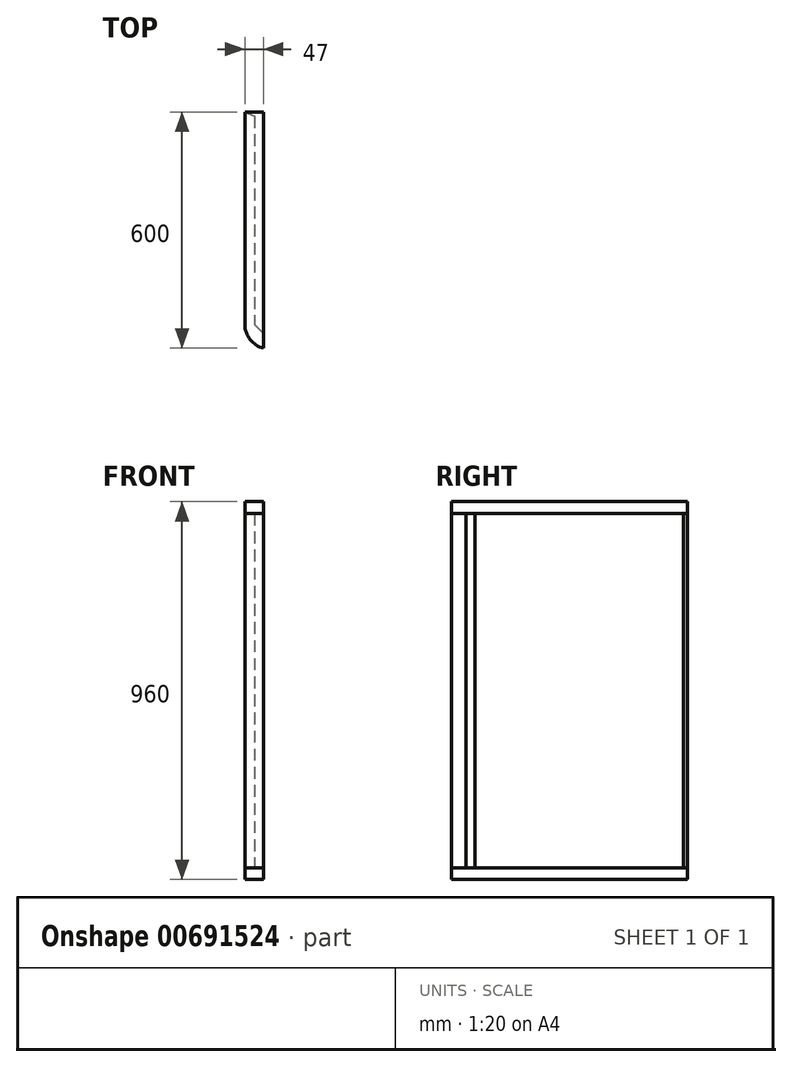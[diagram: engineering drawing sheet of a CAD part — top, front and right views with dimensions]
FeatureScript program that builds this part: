
annotation { "Feature Type Name" : "Feature", "Feature Type Description" : "" }
export const myFeature = defineFeature(function(context is Context, id is Id, definition is map)
    precondition{}
    {
        {
            var Q0;
            Q0=qCreatedBy(makeId("Top.planeOp"),FACE);
            var sketch = newSketch(context, id + "F0", { "sketchPlane" : qUnion([Q0])});
            skLineSegment(sketch, "E0", {"start": v(25, -10.36) * mm, "end": v(25, -540) * mm});
            skLineSegment(sketch, "E1", {"start": v(0, 0) * mm, "end": v(0, -540) * mm});
            skArc(sketch, "E2", {"start": v(0, -540) * mm, "mid": v(13.15, -578.1) * mm, "end": v(47, -600) * mm});
            skLineSegment(sketch, "E3", {"start": v(47, -600) * mm, "end": v(47, -563) * mm});
            skLineSegment(sketch, "E4", {"start": v(25, -540) * mm, "end": v(47, -563) * mm});
            skLineSegment(sketch, "E5", {"start": v(0, 0) * mm, "end": v(25, -10.36) * mm});
            skSolve(sketch);
        }
        {
            var Q0;
            Q0=makeQuery(id+"F0.imprint","IMPRINT",FACE,{"disambiguationData":[TD([[makeQuery(id+"F0.imprint","IMPRINT",EDGE,{"derivedFrom":sQuery(id+"F0.wireOp",EDGE,"E0")}),-1.0]])]});
            extrude(context, id + "F1", {"entities" : qUnion([Q0]), "depth" : 900 * mm, "offsetDistance" : 25 * mm});
        }
        {
            var Q0;
            Q0=makeQuery(id+"F1.opExtrude","CAP_FACE",FACE,{"disambiguationData":[OSD([sQuery(id+"F0.wireOp",EDGE,"E0"),sQuery(id+"F0.wireOp",EDGE,"E1"),sQuery(id+"F0.wireOp",EDGE,"E2"),sQuery(id+"F0.wireOp",EDGE,"E3"),sQuery(id+"F0.wireOp",EDGE,"E4"),sQuery(id+"F0.wireOp",EDGE,"E5")])],"isStart":false});
            var sketch = newSketch(context, id + "F2", { "sketchPlane" : qUnion([Q0])});
            skLineSegment(sketch, "E6.0", {"start": v(0, 0) * mm, "end": v(0, -540) * mm});
            skPoint(sketch, "E7.0", {"position": v(13.15, -578.1) * mm});
            skPoint(sketch, "E8.0", {"position": v(12.5, -5.18) * mm});
            skLineSegment(sketch, "E9.0", {"start": v(0, 0) * mm, "end": v(25, -10.36) * mm});
            skLineSegment(sketch, "E10", {"start": v(0, 0) * mm, "end": v(47, 0) * mm});
            skLineSegment(sketch, "E11", {"start": v(47, -600) * mm, "end": v(47, 0) * mm});
            skSolve(sketch);
        }
        {
            var Q0;
            Q0=makeQuery(id+"F2.imprint","IMPRINT",FACE,{"disambiguationData":[TD([[makeQuery(id+"F2.imprint","IMPRINT",EDGE,{"derivedFrom":sQuery(id+"F2.wireOp",EDGE,"E9.0")}),1.0]])]});
            var Q1;
            Q1=makeQuery(id+"F2.imprint","IMPRINT",FACE,{"disambiguationData":[TD([[makeQuery(id+"F2.imprint","IMPRINT",EDGE,{"derivedFrom":sQuery(id+"F2.wireOp",EDGE,"E6.0")}),1.0]])]});
            extrude(context, id + "F3", {"entities" : qUnion([Q0, Q1]), "depth" : 30 * mm, "offsetDistance" : 25 * mm});
        }
        {
            var Q0;
            Q0=makeQuery(id+"F1.opExtrude","CAP_FACE",FACE,{"disambiguationData":[OSD([sQuery(id+"F0.wireOp",EDGE,"E0"),sQuery(id+"F0.wireOp",EDGE,"E1"),sQuery(id+"F0.wireOp",EDGE,"E2"),sQuery(id+"F0.wireOp",EDGE,"E3"),sQuery(id+"F0.wireOp",EDGE,"E4"),sQuery(id+"F0.wireOp",EDGE,"E5")])],"isStart":false});
            var Q1;
            Q1=makeQuery(id+"F1.opExtrude","CAP_FACE",FACE,{"disambiguationData":[OSD([sQuery(id+"F0.wireOp",EDGE,"E0"),sQuery(id+"F0.wireOp",EDGE,"E1"),sQuery(id+"F0.wireOp",EDGE,"E2"),sQuery(id+"F0.wireOp",EDGE,"E3"),sQuery(id+"F0.wireOp",EDGE,"E4"),sQuery(id+"F0.wireOp",EDGE,"E5")])],"isStart":true});
            cPlane(context, id + "F4", {"entities" : qUnion([Q0, Q1]), "cplaneType" : CPlaneType.MID_PLANE, "offset" : 25 * mm, "width" : 150 * mm, "height" : 150 * mm});
        }
        {
            var Q0;
            Q0=makeQuery(id+"F3.opExtrude","SWEPT_BODY",BODY,{"disambiguationData":[OSD([sQuery(id+"F0.wireOp",EDGE,"E2"),sQuery(id+"F2.wireOp",EDGE,"E6.0"),sQuery(id+"F2.wireOp",EDGE,"E10"),sQuery(id+"F2.wireOp",EDGE,"E11")])]});
            var Q1;
            Q1=qCreatedBy(id+"F4.planeOp",FACE);
            mirror(context, id + "F5", {"entities" : qUnion([Q0]), "mirrorPlane" : qUnion([Q1])});
        }
    });
